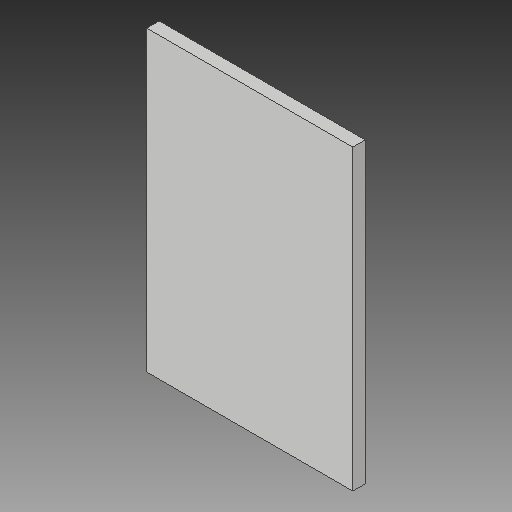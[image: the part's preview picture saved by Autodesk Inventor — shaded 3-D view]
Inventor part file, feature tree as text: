
AUTODESK INVENTOR PART (.ipt)
format: ipt  version: 2018 (Build 220112000, 112)  size: 88,576 bytes
history: native  units: mm
features: other x1, extrude x1
ambient origin geometry x8: Origin, YZ Plane, XZ Plane, XY Plane, X Axis, Y Axis, Z Axis, Center Point
bodies: Body1 (feature_tree)
feature tree (2):
  other  "Sólido1"
  extrude  "Extrusão1"  Depth=6.35mm TaperAngle=0.0deg
